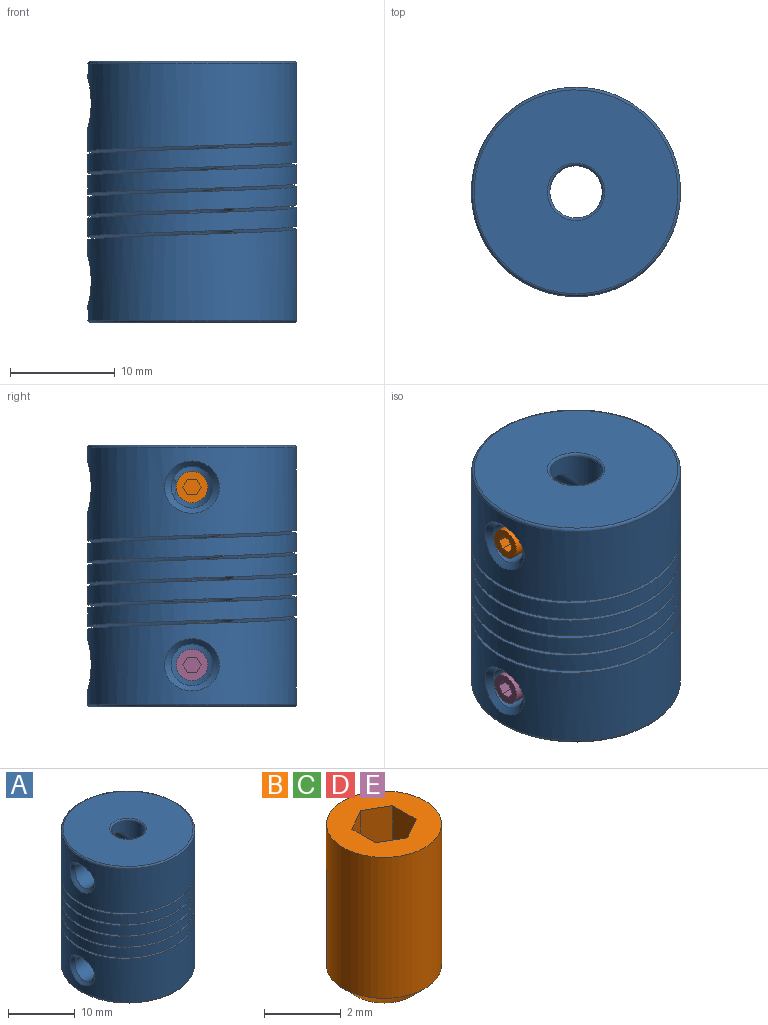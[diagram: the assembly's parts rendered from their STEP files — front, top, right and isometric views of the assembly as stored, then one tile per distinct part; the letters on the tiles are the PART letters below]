
ASSEMBLY  parts=5 mates=4
PART A: 28 faces, bbox 23.5x23.1x25 mm
  f0: cylinder r=4mm len=9.91mm, axis (0,0,-1), area 193.2mm2, adj f1,f12,f13,f15,f16,f20,f22
  f1: cylinder r=4mm len=8mm, axis (0,0,-1), area 43.8mm2, adj f0,f2,f13,f15
  f2: cylinder r=4mm len=8mm, axis (0,0,-1), area 25.1mm2, adj f1,f10,f13,f15
  f3: cylinder r=10mm len=20mm, axis (0,0,-1), area 550.8mm2, adj f6,f12,f13,f15,f18,f24,f25
  f4: cylinder r=10mm len=20mm, axis (0,0,-1), area 594.1mm2, adj f5,f11,f13,f15,f19,f26,f27
  f5: cylinder r=10mm len=20mm, axis (0,0,-1), area 109.4mm2, adj f4,f6,f13,f15
  f6: cylinder r=10mm len=20mm, axis (0,0,-1), area 109.4mm2, adj f3,f5,f13,f15
  f7: plane 19.5x19.5mm, normal (0,0,1), area 274.9mm2, adj f17,f19
  f8: plane 19.5x19.5mm, normal (0,0,-1), area 241.9mm2, adj f16,f18
  f9: cylinder r=2.5mm len=12.25mm, axis (0,0,-1), area 165.8mm2, adj f10,f17,f21,f23
  f10: plane 8x7.66mm, normal (0,0,-1), area 27.4mm2, adj f2,f9,f13,f14,f15
  f11: plane 7.73x5.62mm, normal (-0.59,-0.81,0), area 2.9mm2, adj f4,f13,f14,f15
  f12: plane 6.89x0.3mm, normal (0,1,0), area 2.1mm2, adj f0,f3,f13,f15
  f13: bspline ~23.46x23.09mm, area 1346.3mm2, adj f0,f1,f2,f3,f4,f5,f6,f10
  f14: cylinder r=3mm len=6mm, axis (0,0,1), area 12.9mm2, adj f10,f11,f13,f15
  f15: bspline ~23.46x23.09mm, area 1349.3mm2, adj f0,f1,f2,f3,f4,f5,f6,f10
  f16: torus R=4.25mm, axis (0,0,1), area 10.1mm2, adj f0,f8
  f17: torus R=2.75mm, axis (0,0,1), area 6.4mm2, adj f7,f9
  f18: torus R=9.75mm, axis (0,0,1), area 24.4mm2, adj f3,f8
  f19: torus R=9.75mm, axis (0,0,1), area 24.4mm2, adj f4,f7
  f20: cylinder r=2mm len=5.5mm, axis (0,-1,0), area 69.1mm2, adj f0,f24
  f21: cylinder r=2mm len=7.73mm, axis (0,-1,0), area 93.3mm2, adj f9,f23,f27
  f22: cylinder r=2mm len=5.5mm, axis (1,0,0), area 69.1mm2, adj f0,f25
  f23: cylinder r=2mm len=7.73mm, axis (1,0,0), area 95.5mm2, adj f9,f21,f26
  f24: bspline ~5.26x5mm, area 10.8mm2, adj f3,f20
  f25: bspline ~5.26x5mm, area 10.8mm2, adj f3,f22
  f26: bspline ~5.26x5mm, area 10.8mm2, adj f4,f23
  f27: bspline ~5.26x5mm, area 10.8mm2, adj f4,f21
PART B: 11 faces, bbox 3x3x5 mm
  f0: plane 3x3mm, normal (0,0,1), area 5.1mm2, adj f1,f3,f4,f5,f6,f7,f8
  f1: cylinder r=1.5mm len=4.5mm, axis (0,0,-1), area 42.4mm2, adj f0,f10
  f2: plane 2x2mm, normal (0,0,-1), area 3.1mm2, adj f10
  f3: plane 1.5x0.87mm, normal (-1,0,0), area 1.3mm2, adj f0,f4,f8,f9
  f4: plane 1.5x0.75mm, normal (-0.5,-0.87,0), area 1.3mm2, adj f0,f3,f5,f9
  f5: plane 1.5x0.75mm, normal (0.5,-0.87,0), area 1.3mm2, adj f0,f4,f6,f9
  f6: plane 1.5x0.87mm, normal (1,0,0), area 1.3mm2, adj f0,f5,f7,f9
  f7: plane 1.5x0.75mm, normal (0.5,0.87,0), area 1.3mm2, adj f0,f6,f8,f9
  f8: plane 1.5x0.75mm, normal (-0.5,0.87,0), area 1.3mm2, adj f0,f3,f7,f9
  f9: plane 1.73x1.5mm, normal (0,0,1), area 1.9mm2, adj f3,f4,f5,f6,f7,f8
  f10: cone r=1.5mm half-angle=45deg, axis (0,0,1), area 5.6mm2, adj f1,f2
PART C: same geometry as B
PART D: same geometry as B
PART E: same geometry as B
PLACE A t=(-73.74,20.51,399.7)mm
PLACE B rot(axis=(-0.71,0,0.71),180deg) t=(-78.29,20.51,420.7)mm
PLACE C rot(axis=(-0.58,0.58,0.58),120deg) t=(-73.74,25.05,420.7)mm
PLACE D rot(axis=(-0.58,0.58,0.58),120deg) t=(-73.74,25.04,403.7)mm
PLACE E rot(axis=(-0.71,0,0.71),180deg) t=(-78.28,20.51,403.7)mm
MATE fastened D.f1 <-> A.f20  axis (0,1,0) through (-73.74,30.04,403.7)mm
MATE fastened B.f1 <-> A.f23  axis (1,0,0) through (-83.29,20.51,420.7)mm
MATE fastened C.f1 <-> A.f21  axis (0,-1,0) through (-73.74,30.05,420.7)mm
MATE fastened E.f1 <-> A.f22  axis (-1,0,0) through (-83.28,20.51,403.7)mm
